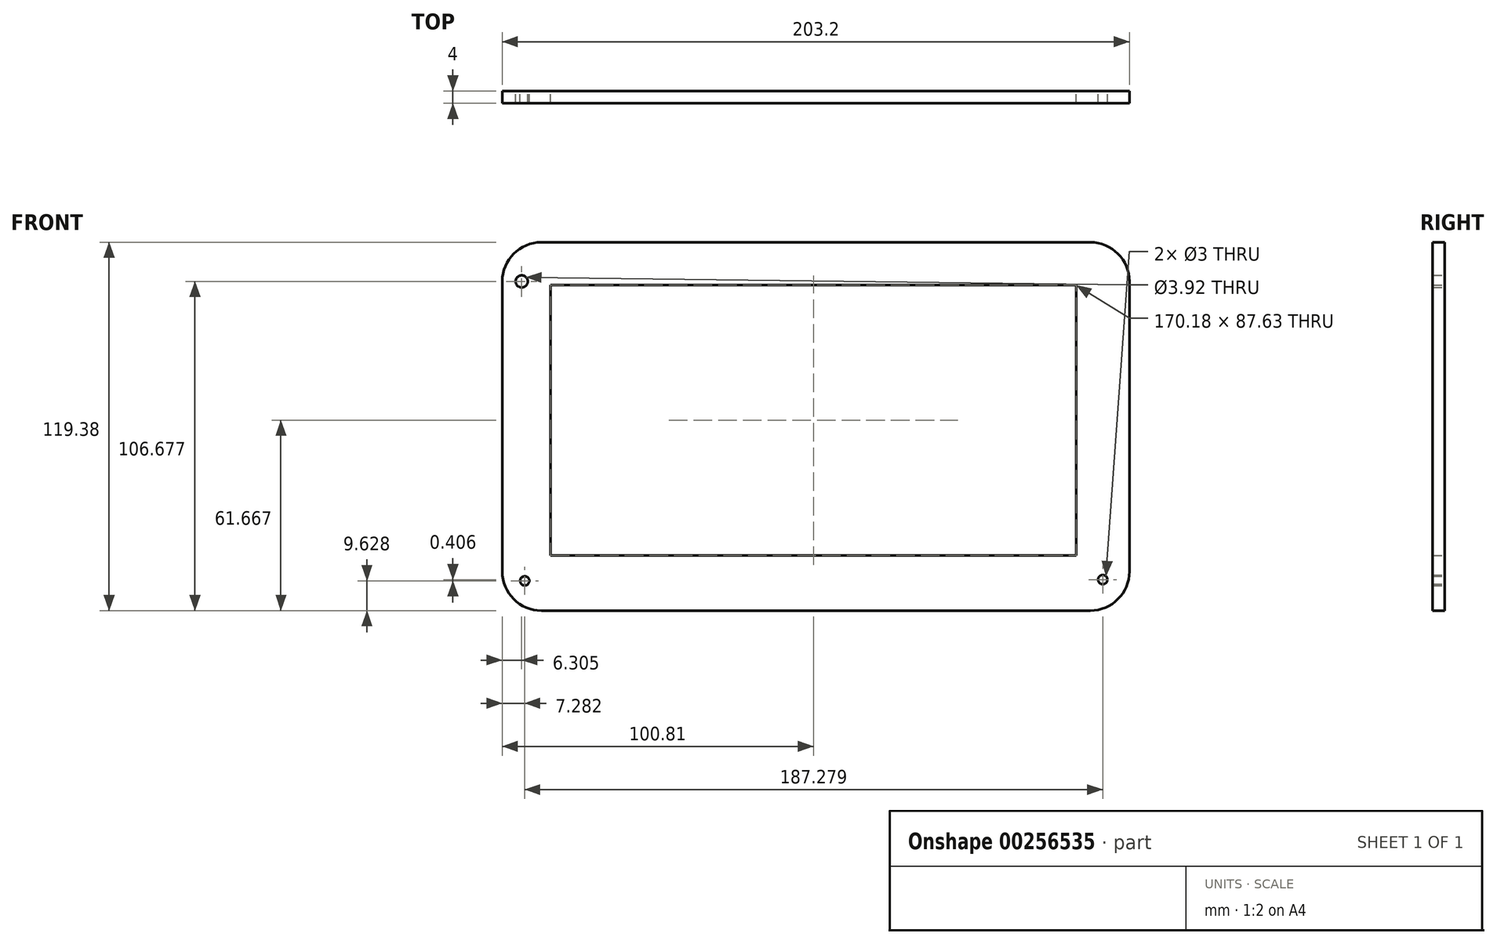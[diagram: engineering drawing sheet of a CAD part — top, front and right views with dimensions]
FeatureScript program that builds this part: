
annotation { "Feature Type Name" : "Feature", "Feature Type Description" : "" }
export const myFeature = defineFeature(function(context is Context, id is Id, definition is map)
    precondition{}
    {
        {
            var Q0;
            Q0=qCreatedBy(makeId("Front.planeOp"),FACE);
            var sketch = newSketch(context, id + "F0", { "sketchPlane" : qUnion([Q0])});
            skLineSegment(sketch, "E0.bottom", {"start": v(-83.85, 69.58) * mm, "end": v(93.95, 69.58) * mm});
            skLineSegment(sketch, "E0.top", {"start": v(-83.85, -49.8) * mm, "end": v(93.95, -49.8) * mm});
            skLineSegment(sketch, "E0.left", {"start": v(-96.55, 56.88) * mm, "end": v(-96.55, -37.1) * mm});
            skLineSegment(sketch, "E0.right", {"start": v(106.65, 56.88) * mm, "end": v(106.65, -37.1) * mm});
            skLineSegment(sketch, "E1.bottom", {"start": v(-80.83, 55.68) * mm, "end": v(89.35, 55.68) * mm});
            skLineSegment(sketch, "E1.top", {"start": v(-80.83, -31.95) * mm, "end": v(89.35, -31.95) * mm});
            skLineSegment(sketch, "E1.left", {"start": v(-80.83, 55.68) * mm, "end": v(-80.83, -31.95) * mm});
            skLineSegment(sketch, "E1.right", {"start": v(89.35, 55.68) * mm, "end": v(89.35, -31.95) * mm});
            skPoint(sketch, "E2.visualSharp", {"position": v(-96.55, 69.58) * mm});
            skArc(sketch, "E2.filletArc", {"start": v(-83.85, 69.58) * mm, "mid": v(-92.83, 65.86) * mm, "end": v(-96.55, 56.88) * mm});
            skPoint(sketch, "E3.visualSharp", {"position": v(-96.55, -49.8) * mm});
            skArc(sketch, "E3.filletArc", {"start": v(-96.55, -37.1) * mm, "mid": v(-92.83, -46.08) * mm, "end": v(-83.85, -49.8) * mm});
            skPoint(sketch, "E4.visualSharp", {"position": v(106.65, -49.8) * mm});
            skArc(sketch, "E4.filletArc", {"start": v(93.95, -49.8) * mm, "mid": v(102.93, -46.08) * mm, "end": v(106.65, -37.1) * mm});
            skPoint(sketch, "E5.visualSharp", {"position": v(106.65, 69.58) * mm});
            skArc(sketch, "E5.filletArc", {"start": v(106.65, 56.88) * mm, "mid": v(102.93, 65.86) * mm, "end": v(93.95, 69.58) * mm});
            skPoint(sketch, "E6.visualSharp", {"position": v(-80.83, 55.68) * mm});
            skLineSegment(sketch, "E6.filletArc", {"start": v(-80.83, 55.68) * mm, "end": v(-80.83, 55.68) * mm});
            skCircle(sketch, "E7", {"center": v(-90.24, 56.88) * mm, "radius": 1.96 * mm});
            skCircle(sketch, "E8", {"center": v(-89.27, -40.17) * mm, "radius": 1.5 * mm});
            skCircle(sketch, "E9", {"center": v(98.01, -39.77) * mm, "radius": 1.5 * mm});
            skSolve(sketch);
        }
        {
            var Q0;
            Q0 = qSketchRegion(id + "F0", true);
            extrude(context, id + "F1", {"entities" : qUnion([Q0]), "depth" : 4 * mm});
        }
    });
